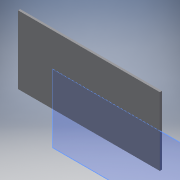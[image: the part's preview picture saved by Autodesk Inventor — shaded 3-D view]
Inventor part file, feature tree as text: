
AUTODESK INVENTOR PART (.ipt)
format: ipt  version: 2017 (Build 210142000, 142)  size: 101,376 bytes
history: native  units: in
note: dims shown in document units (in); Inventor stores cm internally (conversion verified against a paired STEP export)
features: extrude x2, sketch x2
ambient origin geometry x8: Origin, YZ Plane, XZ Plane, XY Plane, X Axis, Y Axis, Z Axis, Center Point
bodies: Solid1 (feature_tree)
feature tree (4):
  extrude  "Extrusion1"  Depth=2.5197in
  extrude  "Extrusion2"  Depth=1.1811in
  sketch  "Sketch1"  dims[d0=5.2362in d1=2.5197in]
  sketch  "Sketch2"  dims[d2=0.0787in d3=0.0in d6=1.1811in d7=0.1181in d12=1.1811in d13=0.1378in d14=0.1181in d15=0.0in]
